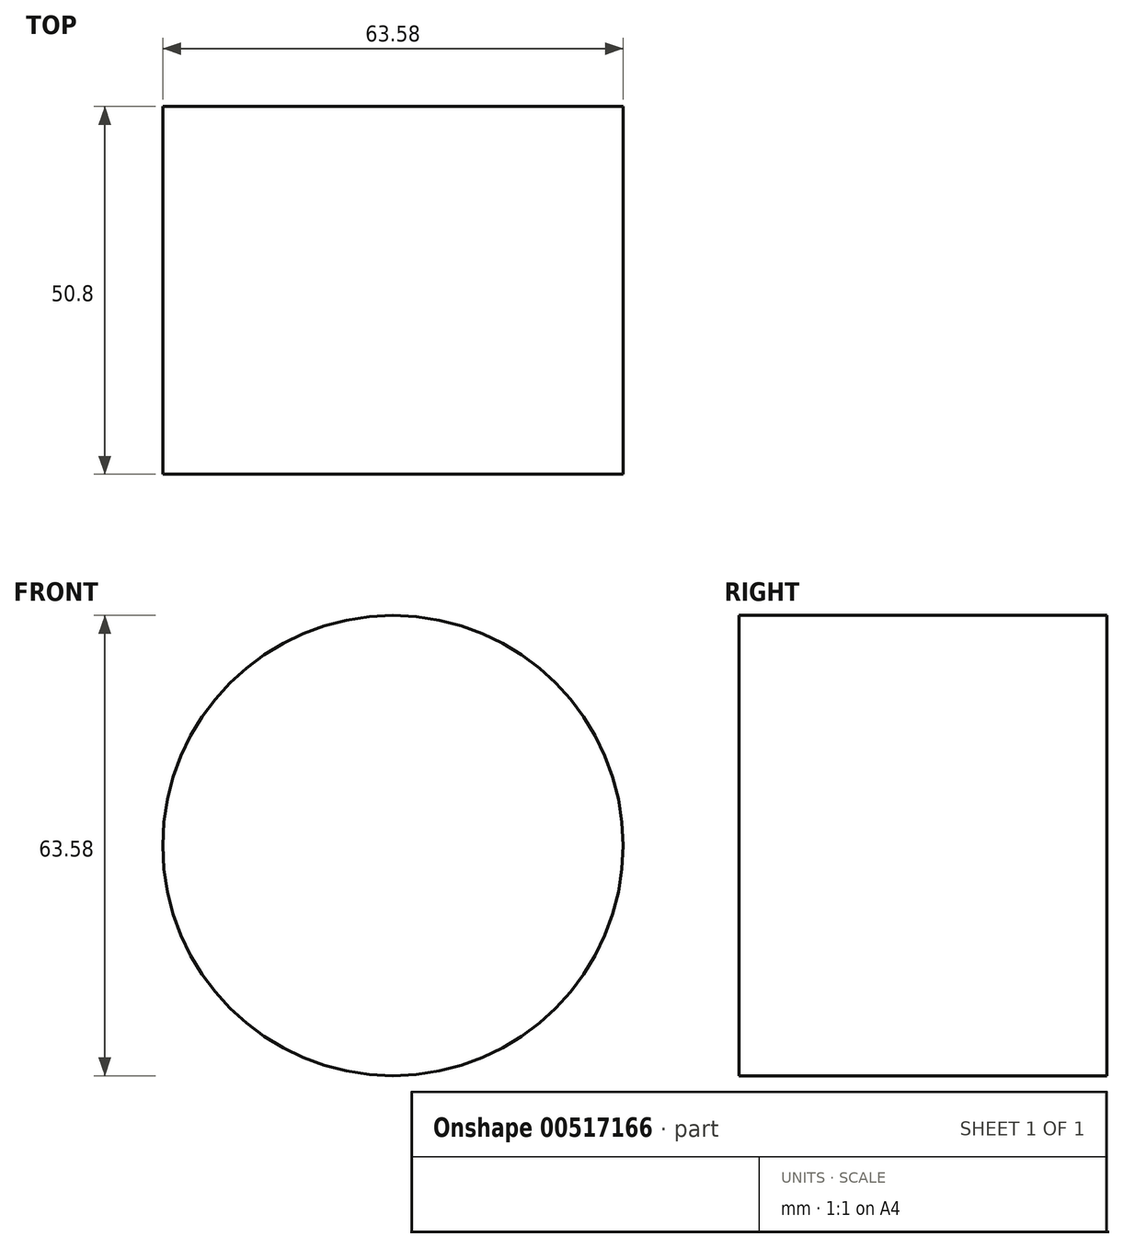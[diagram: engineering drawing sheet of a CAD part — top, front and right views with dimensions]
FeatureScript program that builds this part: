
annotation { "Feature Type Name" : "Feature", "Feature Type Description" : "" }
export const myFeature = defineFeature(function(context is Context, id is Id, definition is map)
    precondition{}
    {
        {
            var Q0;
            Q0=qCreatedBy(makeId("Front.planeOp"),FACE);
            var sketch = newSketch(context, id + "F0", { "sketchPlane" : qUnion([Q0])});
            skCircle(sketch, "E0", {"center": v(0, 0) * mm, "radius": 31.79 * mm});
            skSolve(sketch);
        }
        {
            var Q0;
            Q0=makeQuery(id+"F0.imprint","IMPRINT",FACE,{"disambiguationData":[TD([[makeQuery(id+"F0.imprint","IMPRINT",EDGE,{"derivedFrom":sQuery(id+"F0.wireOp",EDGE,"E0")}),1.0]])]});
            extrude(context, id + "F1", {"entities" : qUnion([Q0]), "depth" : 50.8 * mm, "offsetDistance" : 25.4 * mm});
        }
    });
